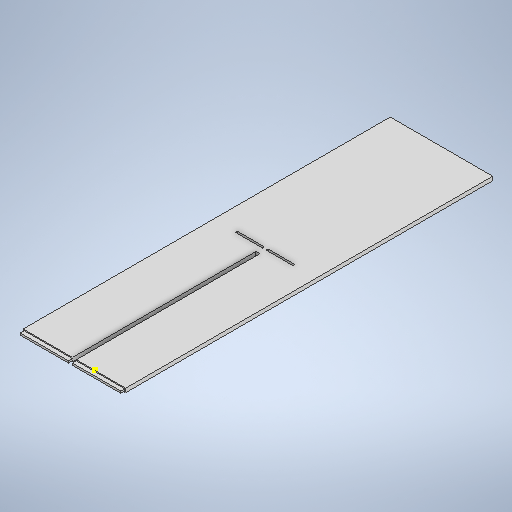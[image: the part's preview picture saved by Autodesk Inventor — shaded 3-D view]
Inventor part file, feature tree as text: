
AUTODESK INVENTOR PART (.ipt)
format: ipt  version: 2025.2 (Build 292293000, 293)  size: 376,320 bytes
history: native  units: mm
features: sketch x13, extrude x12, projected_geometry x3
ambient origin geometry x8: Origin, YZ Plane, XZ Plane, XY Plane, X Axis, Y Axis, Z Axis, Center Point
bodies: Solid1 (feature_tree)
feature tree (28):
  extrude  "Extrusion1"  Depth=447.675mm
  extrude  "Extrusion2"  Depth=4.7625mm TaperAngle=0.0deg
  extrude  "Extrusion3"  Depth=10.0mm TaperAngle=0.0deg
  extrude  "Extrusion4"  Depth=158.838mm TaperAngle=0.0deg
  sketch  "Sketch5"  dims[d25=4.763mm d26=223.837mm d27=0.0mm]
  extrude  "Extrusion5"  Depth=223.837mm TaperAngle=0.0deg
  extrude  "Extrusion6"  Depth=15.0mm TaperAngle=0.0deg
  extrude  "Extrusion7"  Depth=2.374mm TaperAngle=0.0deg
  extrude  "Extrusion8"  Depth=37.5mm
  extrude  "Extrusion9"  Depth=10.0mm TaperAngle=0.0deg
  extrude  "Extrusion10"  Depth=32.503mm TaperAngle=0.0deg
  extrude  "Extrusion11"  [1 undecoded]
  extrude  "Extrusion12"  [1 undecoded]
  sketch  "Sketch1"  dims[d0=50.0mm d1=447.675mm]
  sketch  "Sketch2"  dims[d2=4.7625mm d3=0.0mm d9=4.7625mm d10=0.0mm]
  sketch  "Sketch3"  dims[d11=25.0mm d18=10.0mm d19=0.0mm]
  sketch  "Sketch4"  dims[d20=10.0mm d21=0.0mm d22=158.838mm d23=0.0mm]
  sketch  "Sketch6"  dims[d28=15.0mm d29=0.0mm d30=15.0mm d31=0.0mm]
  projected_geometry  "Projected Loop1"
  sketch  "Sketch8"  dims[d35=2.374mm d36=10.0mm d37=0.0mm]
  sketch  "Sketch9"  dims[d39=37.5mm d40=37.5mm]
  projected_geometry  "Projected Loop2"
  sketch  "Sketch10"  dims[d41=10.0mm d42=0.0mm d44=10.0mm d45=0.0mm]
  projected_geometry  "Projected Loop3"
  sketch  "Sketch14"  dims[d47=32.503mm d48=10.0mm d49=0.0mm]
  sketch  "Sketch17"
  sketch  "Sketch18"
  sketch  "Sketch19"
note: 2 required parameter values undecoded (feature->parameter linkage not recoverable at this tier; creation-order binding heuristic only, values carry confidence <= 0.55)
